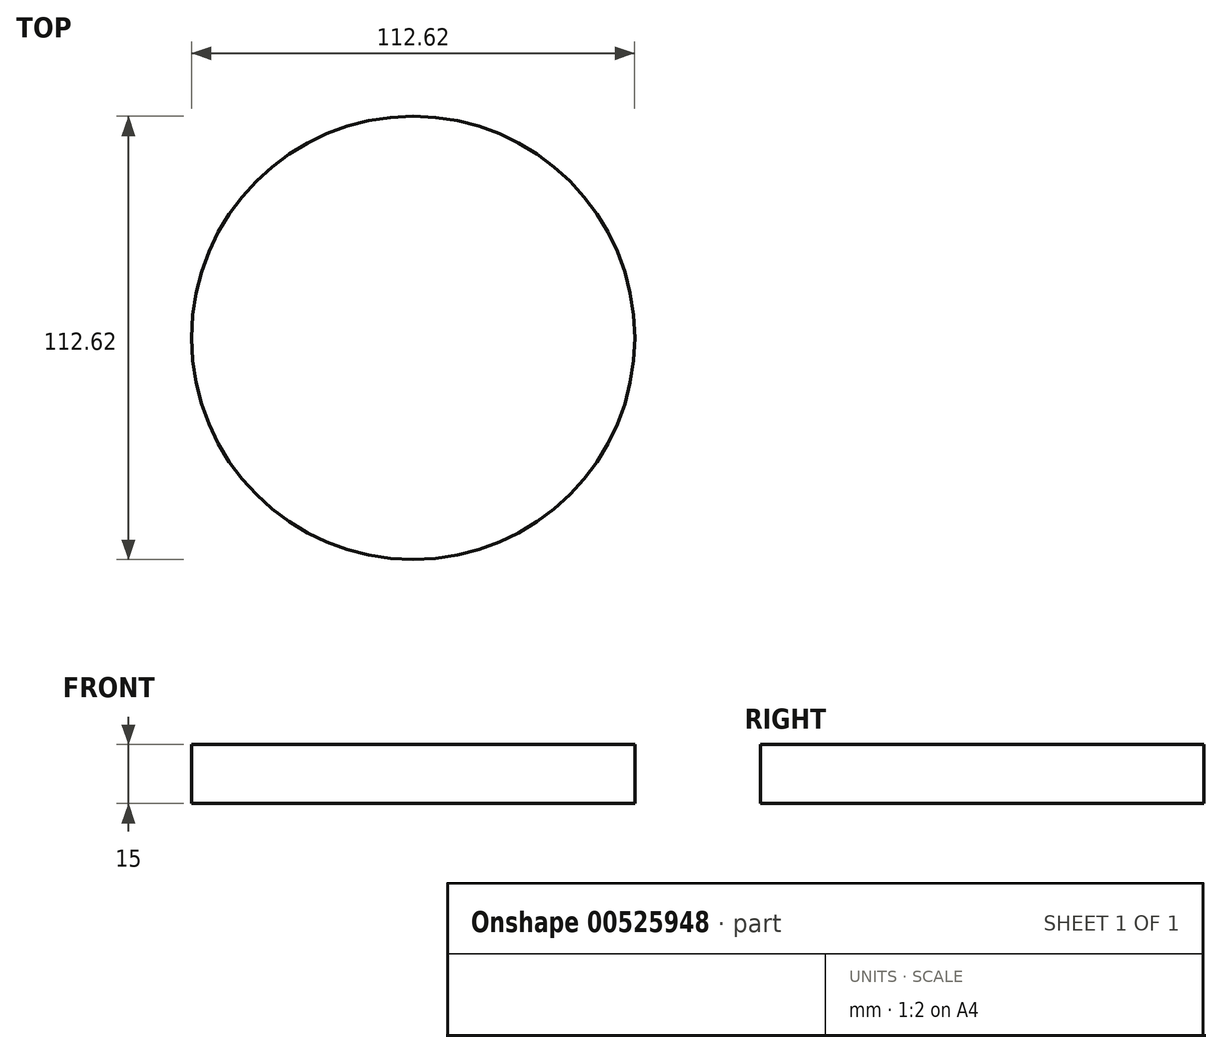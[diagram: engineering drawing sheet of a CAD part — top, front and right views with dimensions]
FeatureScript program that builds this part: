
annotation { "Feature Type Name" : "Feature", "Feature Type Description" : "" }
export const myFeature = defineFeature(function(context is Context, id is Id, definition is map)
    precondition{}
    {
        {
            var Q0;
            Q0=qCreatedBy(makeId("Top.planeOp"),FACE);
            var sketch = newSketch(context, id + "F0", { "sketchPlane" : qUnion([Q0])});
            skCircle(sketch, "E0", {"center": v(0, 0) * mm, "radius": 56.31 * mm});
            skSolve(sketch);
        }
        {
            var Q0;
            Q0=makeQuery(id+"F0.imprint","IMPRINT",FACE,{"disambiguationData":[TD([[makeQuery(id+"F0.imprint","IMPRINT",EDGE,{"derivedFrom":sQuery(id+"F0.wireOp",EDGE,"E0")}),1.0]])]});
            extrude(context, id + "F1", {"entities" : qUnion([Q0]), "depth" : 15 * mm, "offsetDistance" : 25.4 * mm});
        }
    });
